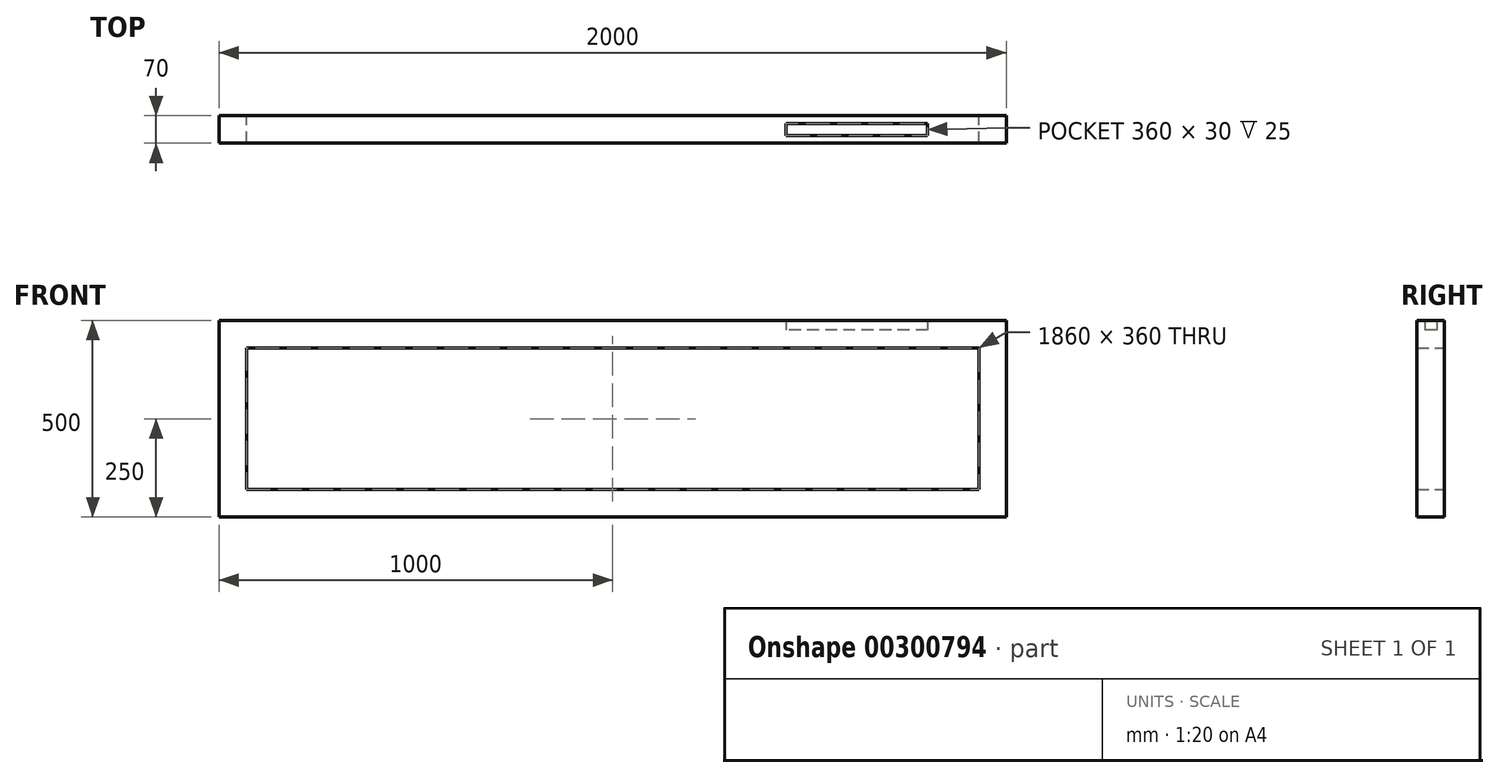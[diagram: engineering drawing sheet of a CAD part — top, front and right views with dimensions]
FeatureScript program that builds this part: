
annotation { "Feature Type Name" : "Feature", "Feature Type Description" : "" }
export const myFeature = defineFeature(function(context is Context, id is Id, definition is map)
    precondition{}
    {
        {
            var Q0;
            Q0=qCreatedBy(makeId("Front.planeOp"),FACE);
            var sketch = newSketch(context, id + "F0", { "sketchPlane" : qUnion([Q0])});
            skLineSegment(sketch, "E0.bottom", {"start": v(0, 0) * mm, "end": v(2000, 0) * mm});
            skLineSegment(sketch, "E0.top", {"start": v(0, -500) * mm, "end": v(2000, -500) * mm});
            skLineSegment(sketch, "E0.left", {"start": v(0, 0) * mm, "end": v(0, -500) * mm});
            skLineSegment(sketch, "E0.right", {"start": v(2000, 0) * mm, "end": v(2000, -500) * mm});
            skLineSegment(sketch, "E1", {"start": v(70, 0) * mm, "end": v(70, -500) * mm});
            skLineSegment(sketch, "E2", {"start": v(0, -70) * mm, "end": v(2000, -70) * mm});
            skLineSegment(sketch, "E3", {"start": v(1930, 0) * mm, "end": v(1930, -500) * mm});
            skLineSegment(sketch, "E4", {"start": v(0, -430) * mm, "end": v(2000, -430) * mm});
            skSolve(sketch);
        }
        {
            var Q0;
            Q0 = qSketchRegion(id + "F0", true);
            extrude(context, id + "F1", {"entities" : qUnion([Q0]), "depth" : 70 * mm});
        }
        {
            var Q0;
            Q0=makeQuery(id+"F1.opExtrude","SWEPT_FACE",FACE,{"disambiguationData":[OSD([sQuery(id+"F0.wireOp",EDGE,"E0.bottom")])]});
            var sketch = newSketch(context, id + "F2", { "sketchPlane" : qUnion([Q0])});
            skLineSegment(sketch, "E5.bottom", {"start": v(1800, -20) * mm, "end": v(1440, -20) * mm});
            skLineSegment(sketch, "E5.top", {"start": v(1800, -50) * mm, "end": v(1440, -50) * mm});
            skLineSegment(sketch, "E5.left", {"start": v(1800, -20) * mm, "end": v(1800, -50) * mm});
            skLineSegment(sketch, "E5.right", {"start": v(1440, -20) * mm, "end": v(1440, -50) * mm});
            skSolve(sketch);
        }
        {
            var Q0;
            Q0=makeQuery(id+"F2.imprint","IMPRINT",FACE,{"disambiguationData":[TD([[makeQuery(id+"F2.imprint","IMPRINT",EDGE,{"derivedFrom":sQuery(id+"F2.wireOp",EDGE,"E5.bottom")}),1.0]])]});
            extrude(context, id + "F3", {"entities" : qUnion([Q0]), "operationType" : NewBodyOperationType.REMOVE, "depth" : 25 * mm, "hasSecondDirection" : true, "secondDirectionOppositeDirection" : true, "secondDirectionDepth" : 25 * mm});
        }
    });
